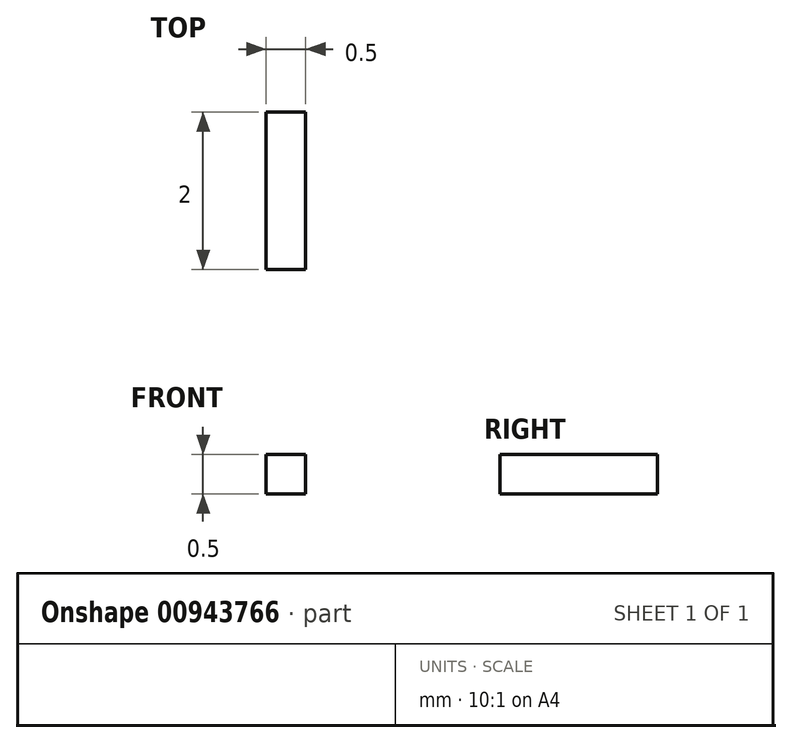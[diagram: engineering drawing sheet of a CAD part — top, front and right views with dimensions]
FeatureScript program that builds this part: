
annotation { "Feature Type Name" : "Feature", "Feature Type Description" : "" }
export const myFeature = defineFeature(function(context is Context, id is Id, definition is map)
    precondition{}
    {
        {
            var Q0;
            Q0=qCreatedBy(makeId("Front.planeOp"),FACE);
            var sketch = newSketch(context, id + "F0", { "sketchPlane" : qUnion([Q0])});
            skLineSegment(sketch, "E0.bottom", {"start": v(0.25, -0.25) * mm, "end": v(-0.25, -0.25) * mm});
            skLineSegment(sketch, "E0.top", {"start": v(0.25, 0.25) * mm, "end": v(-0.25, 0.25) * mm});
            skLineSegment(sketch, "E0.left", {"start": v(0.25, -0.25) * mm, "end": v(0.25, 0.25) * mm});
            skLineSegment(sketch, "E0.right", {"start": v(-0.25, -0.25) * mm, "end": v(-0.25, 0.25) * mm});
            skPoint(sketch, "E0.middle", {"position": v(0, 0) * mm});
            skSolve(sketch);
        }
        {
            var Q0;
            Q0=makeQuery(id+"F0.imprint","IMPRINT",FACE,{"disambiguationData":[TD([[makeQuery(id+"F0.imprint","IMPRINT",EDGE,{"derivedFrom":sQuery(id+"F0.wireOp",EDGE,"E0.bottom")}),-1.0]])]});
            extrude(context, id + "F1", {"entities" : qUnion([Q0]), "depth" : 2 * mm, "offsetDistance" : 25 * mm, "symmetric" : true});
        }
    });
